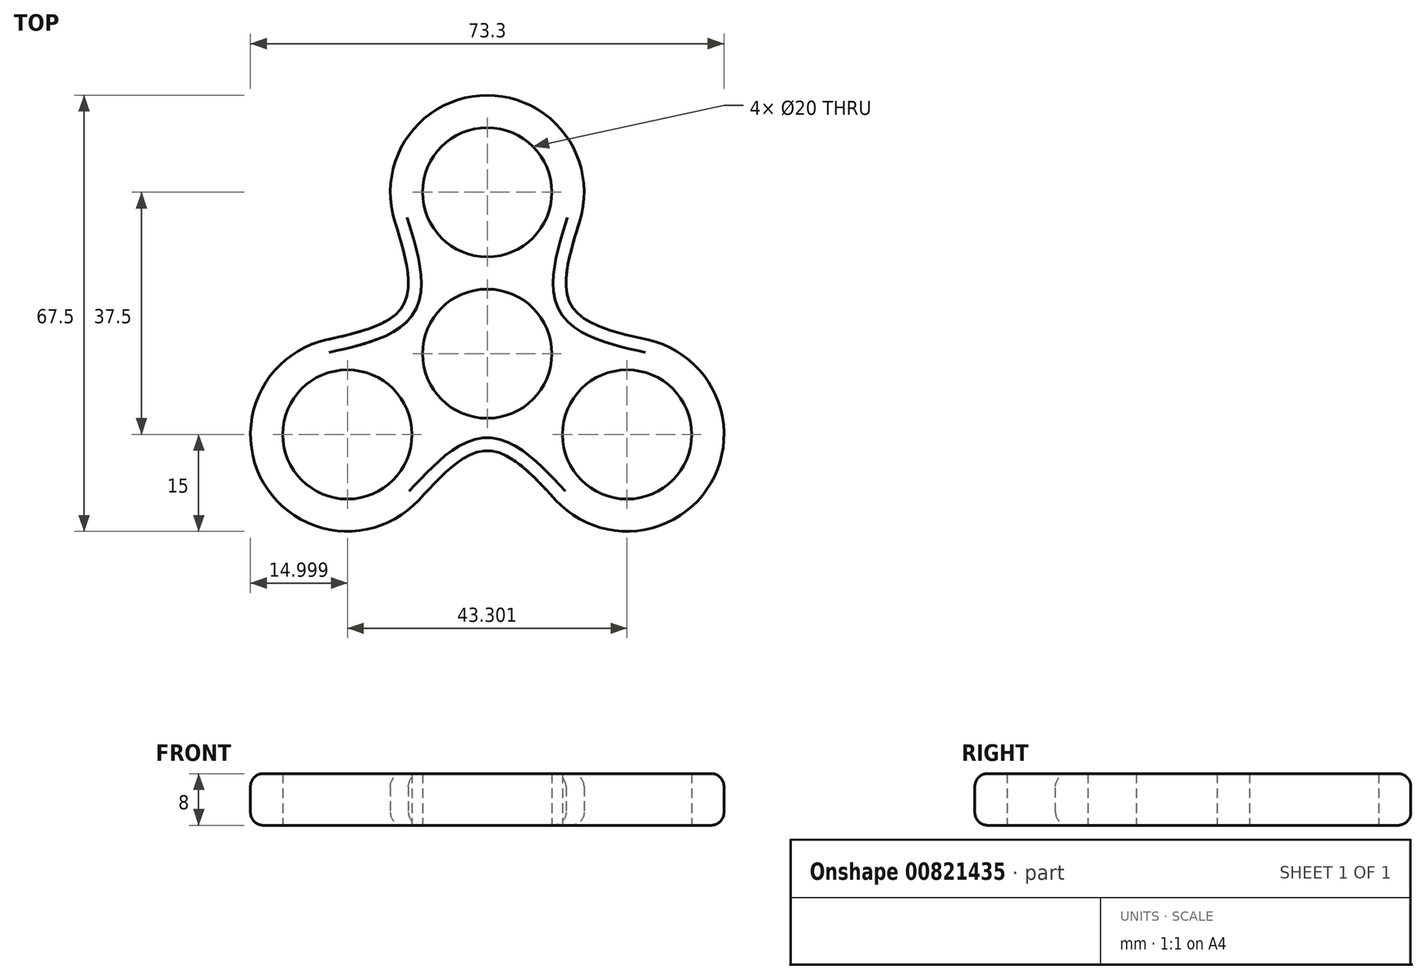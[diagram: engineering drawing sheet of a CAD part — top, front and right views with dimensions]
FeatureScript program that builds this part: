
annotation { "Feature Type Name" : "Feature", "Feature Type Description" : "" }
export const myFeature = defineFeature(function(context is Context, id is Id, definition is map)
    precondition{}
    {
        {
            var Q0;
            Q0=qCreatedBy(makeId("Top.planeOp"),FACE);
            var sketch = newSketch(context, id + "F0", { "sketchPlane" : qUnion([Q0])});
            skLineSegment(sketch, "E0", {"start": v(0, 0) * mm, "end": v(0, 107.39) * mm, "construction": true});
            skLineSegment(sketch, "E1", {"start": v(0, 0) * mm, "end": v(77, -44.46) * mm, "construction": true});
            skLineSegment(sketch, "E2", {"start": v(0, 0) * mm, "end": v(-88.54, -51.12) * mm, "construction": true});
            skCircle(sketch, "E3", {"center": v(0, 0) * mm, "radius": 10 * mm});
            skCircle(sketch, "E4", {"center": v(0, 0) * mm, "radius": 25 * mm, "construction": true});
            skPoint(sketch, "E5", {"position": v(0, 25) * mm});
            skPoint(sketch, "E6", {"position": v(-21.65, -12.5) * mm});
            skPoint(sketch, "E7", {"position": v(21.65, -12.5) * mm});
            skCircle(sketch, "E8", {"center": v(0, 25) * mm, "radius": 10 * mm});
            skCircle(sketch, "E9", {"center": v(-21.65, -12.5) * mm, "radius": 10 * mm});
            skCircle(sketch, "E10", {"center": v(21.65, -12.5) * mm, "radius": 10 * mm});
            skCircle(sketch, "E11", {"center": v(0, 25) * mm, "radius": 15 * mm});
            skCircle(sketch, "E12", {"center": v(21.65, -12.5) * mm, "radius": 15 * mm});
            skCircle(sketch, "E13", {"center": v(-21.65, -12.5) * mm, "radius": 15 * mm});
            skCircle(sketch, "E14", {"center": v(0, 0) * mm, "radius": 15 * mm, "construction": true});
            skLineSegment(sketch, "E15", {"start": v(0, 0) * mm, "end": v(-65.45, 37.79) * mm, "construction": true});
            skLineSegment(sketch, "E16", {"start": v(0, 0) * mm, "end": v(55.55, 32.07) * mm, "construction": true});
            skLineSegment(sketch, "E17", {"start": v(0, 0) * mm, "end": v(0, -65.82) * mm, "construction": true});
            skPoint(sketch, "E18", {"position": v(14.3, 20.5) * mm});
            skPoint(sketch, "E19", {"position": v(13, 7.5) * mm});
            skPoint(sketch, "E20", {"position": v(24.9, 2.14) * mm});
            skPoint(sketch, "E21", {"position": v(10.6, -22.64) * mm});
            skPoint(sketch, "E22", {"position": v(0, -15) * mm});
            skPoint(sketch, "E23", {"position": v(-10.6, -22.64) * mm});
            skPoint(sketch, "E24", {"position": v(-24.9, 2.14) * mm});
            skPoint(sketch, "E25", {"position": v(-13, 7.5) * mm});
            skPoint(sketch, "E26", {"position": v(-14.3, 20.5) * mm});
            skFitSpline(sketch, "E27", {"points": [v(24.9, 2.14) * mm, v(13, 7.5) * mm, v(14.3, 20.5) * mm], "startDerivative": vector(-30.45, 6.9) * mm, "endDerivative": vector(9.26, 29.82) * mm});
            skFitSpline(sketch, "E28", {"points": [v(10.6, -22.64) * mm, v(0, -15) * mm, v(-10.6, -22.64) * mm], "startDerivative": vector(-21.2, 22.93) * mm, "endDerivative": vector(-21.2, -22.93) * mm});
            skFitSpline(sketch, "E29", {"points": [v(-14.3, 20.5) * mm, v(-13, 7.5) * mm, v(-24.9, 2.14) * mm], "startDerivative": vector(9.26, -29.82) * mm, "endDerivative": vector(-30.45, -6.9) * mm});
            skSolve(sketch);
        }
        {
            var Q0;
            Q0 = qSketchRegion(id + "F0", true);
            extrude(context, id + "F1", {"entities" : qUnion([Q0]), "depth" : 8 * mm, "offsetDistance" : 25 * mm});
        }
        {
            var Q0;
            Q0=makeQuery(id+"F1.opExtrude","CAP_EDGE",EDGE,{"disambiguationData":[OSD([sQuery(id+"F0.wireOp",EDGE,"E11")])],"isStart":false});
            var Q1;
            Q1=makeQuery(id+"F1.opExtrude","CAP_EDGE",EDGE,{"disambiguationData":[OSD([sQuery(id+"F0.wireOp",EDGE,"E13")])],"isStart":false});
            var Q2;
            Q2=makeQuery(id+"F1.opExtrude","CAP_EDGE",EDGE,{"disambiguationData":[OSD([sQuery(id+"F0.wireOp",EDGE,"E12")])],"isStart":false});
            fillet(context, id + "F2", {"entities" : qUnion([Q0, Q1, Q2]), "radius" : 2 * mm, "tangentPropagation" : true, "allowEdgeOverflow" : false});
        }
        {
            var Q0;
            Q0=makeQuery(id+"F1.opExtrude","CAP_EDGE",EDGE,{"disambiguationData":[OSD([sQuery(id+"F0.wireOp",EDGE,"E11")])],"isStart":true});
            var Q1;
            Q1=makeQuery(id+"F1.opExtrude","CAP_EDGE",EDGE,{"disambiguationData":[OSD([sQuery(id+"F0.wireOp",EDGE,"E13")])],"isStart":true});
            var Q2;
            Q2=makeQuery(id+"F1.opExtrude","CAP_EDGE",EDGE,{"disambiguationData":[OSD([sQuery(id+"F0.wireOp",EDGE,"E12")])],"isStart":true});
            fillet(context, id + "F3", {"entities" : qUnion([Q0, Q1, Q2]), "radius" : 2 * mm, "tangentPropagation" : true, "allowEdgeOverflow" : false});
        }
    });
